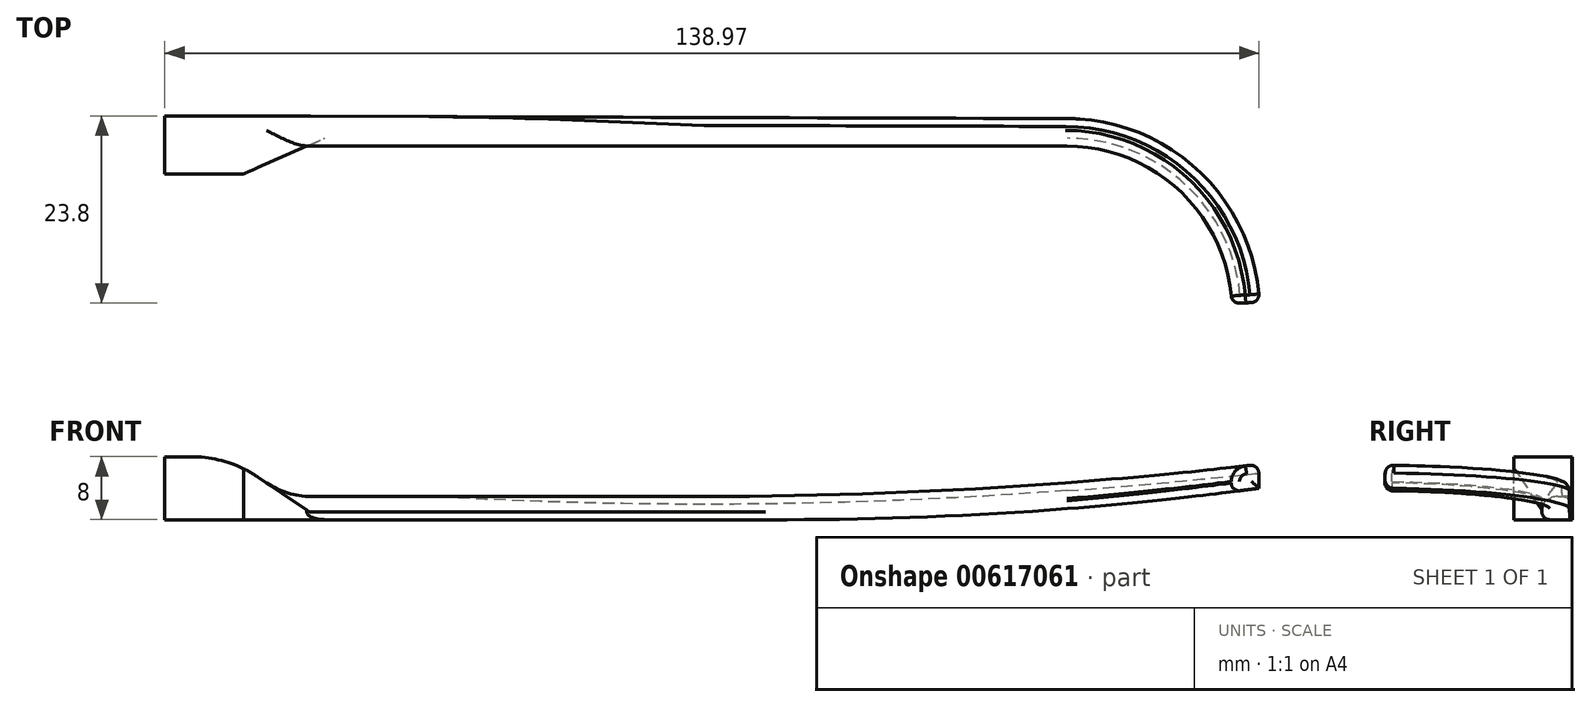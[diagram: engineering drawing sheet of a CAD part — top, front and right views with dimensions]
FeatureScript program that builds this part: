
annotation { "Feature Type Name" : "Feature", "Feature Type Description" : "" }
export const myFeature = defineFeature(function(context is Context, id is Id, definition is map)
    precondition{}
    {
        {
            var Q0;
            Q0=qCreatedBy(makeId("Front.planeOp"),FACE);
            var sketch = newSketch(context, id + "F0", { "sketchPlane" : qUnion([Q0])});
            skLineSegment(sketch, "E0.bottom", {"start": v(0, 0) * mm, "end": v(156.1, 0) * mm});
            skLineSegment(sketch, "E0.top", {"start": v(0, -43.39) * mm, "end": v(156.1, -43.39) * mm});
            skLineSegment(sketch, "E0.left", {"start": v(0, 0) * mm, "end": v(0, -43.39) * mm});
            skLineSegment(sketch, "E0.right", {"start": v(156.1, 0) * mm, "end": v(156.1, -43.39) * mm});
            skSolve(sketch);
        }
        {
            var Q0;
            Q0=qSketchRegion(id+"F0",true);
            extrude(context, id + "F1", {"entities" : qUnion([Q0]), "depth" : 50 * mm, "offsetDistance" : 25 * mm});
        }
        {
            var Q0;
            Q0=makeQuery(id+"F1.opExtrude","CAP_FACE",FACE,{"disambiguationData":[OSD([sQuery(id+"F0.wireOp",EDGE,"E0.bottom"),sQuery(id+"F0.wireOp",EDGE,"E0.top"),sQuery(id+"F0.wireOp",EDGE,"E0.left"),sQuery(id+"F0.wireOp",EDGE,"E0.right")])],"isStart":true});
            var sketch = newSketch(context, id + "F2", { "sketchPlane" : qUnion([Q0])});
            skLineSegment(sketch, "E1.bottom", {"start": v(-156.1, 0) * mm, "end": v(0, 0) * mm});
            skLineSegment(sketch, "E1.top", {"start": v(-156.1, -43.39) * mm, "end": v(0, -43.39) * mm});
            skLineSegment(sketch, "E1.left", {"start": v(-156.1, 0) * mm, "end": v(-156.1, -43.39) * mm});
            skLineSegment(sketch, "E1.right", {"start": v(0, 0) * mm, "end": v(0, -3.74) * mm});
            skLineSegment(sketch, "E2.trimOffspring", {"start": v(0, -25.02) * mm, "end": v(0, -43.39) * mm});
            skLineSegment(sketch, "E3.MirrorCS", {"start": v(0, -11.74) * mm, "end": v(-79.05, -11.74) * mm});
            skLineSegment(sketch, "E4.MirrorCS", {"start": v(-8, -3.74) * mm, "end": v(0, -3.74) * mm});
            skLineSegment(sketch, "E5.MirrorCS", {"start": v(-15.5, -8.8) * mm, "end": v(-8, -3.74) * mm});
            skLineSegment(sketch, "E6.MirrorCS", {"start": v(-68.52, -8.8) * mm, "end": v(-15.5, -8.8) * mm});
            skArc(sketch, "E7.MirrorCS", {"start": v(-68.52, -8.8) * mm, "mid": v(-104.19, -7.75) * mm, "end": v(-139.74, -4.62) * mm});
            skArc(sketch, "E8.MirrorCS", {"start": v(-79.05, -11.74) * mm, "mid": v(-109.6, -10.7) * mm, "end": v(-140, -7.61) * mm});
            skLineSegment(sketch, "E9.MirrorCS", {"start": v(-140, -7.61) * mm, "end": v(-139.74, -4.62) * mm});
            skLineSegment(sketch, "E10.trimOffspring", {"start": v(0, -11.74) * mm, "end": v(0, -25.02) * mm});
            skSolve(sketch);
        }
        {
            var Q0;
            Q0=qSketchRegion(id+"F2",true);
            extrude(context, id + "F3", {"entities" : qUnion([Q0]), "operationType" : NewBodyOperationType.REMOVE, "endBound" : BoundingType.THROUGH_ALL, "oppositeDirection" : true, "depth" : 25 * mm, "offsetDistance" : 25 * mm});
        }
        {
            var Q0;
            Q0=qCreatedBy(makeId("Top.planeOp"),FACE);
            var sketch = newSketch(context, id + "F4", { "sketchPlane" : qUnion([Q0])});
            skLineSegment(sketch, "E11", {"start": v(0, -7.38) * mm, "end": v(10, -7.38) * mm});
            skLineSegment(sketch, "E12", {"start": v(10, -7.38) * mm, "end": v(18.04, -3.85) * mm});
            skLineSegment(sketch, "E13", {"start": v(18.04, -3.85) * mm, "end": v(114.57, -3.85) * mm});
            skArc(sketch, "E14", {"start": v(135.54, -23.84) * mm, "mid": v(129.05, -9.65) * mm, "end": v(114.57, -3.85) * mm});
            skArc(sketch, "E15.0", {"start": v(139.03, -23.68) * mm, "mid": v(131.47, -7.12) * mm, "end": v(114.57, -0.35) * mm});
            skLineSegment(sketch, "E16", {"start": v(135.54, -23.84) * mm, "end": v(139.03, -23.68) * mm});
            skLineSegment(sketch, "E17", {"start": v(114.57, -0.35) * mm, "end": v(0, 0) * mm});
            skLineSegment(sketch, "E18.0", {"start": v(78.92, 0) * mm, "end": v(140, 0) * mm});
            skLineSegment(sketch, "E19.0", {"start": v(0, 0) * mm, "end": v(78.92, 0) * mm});
            skLineSegment(sketch, "E20.0", {"start": v(140, -50) * mm, "end": v(140, 0) * mm});
            skLineSegment(sketch, "E21.0", {"start": v(0, -50) * mm, "end": v(140, -50) * mm});
            skLineSegment(sketch, "E22.0", {"start": v(0, -50) * mm, "end": v(0, -50) * mm});
            skLineSegment(sketch, "E23.0", {"start": v(0, -50) * mm, "end": v(0, -7.38) * mm});
            skSolve(sketch);
        }
        {
            var Q0;
            Q0=qSketchRegion(id+"F4",true);
            extrude(context, id + "F5", {"entities" : qUnion([Q0]), "operationType" : NewBodyOperationType.REMOVE, "oppositeDirection" : true, "depth" : 25 * mm, "offsetDistance" : 25 * mm});
        }
        {
            var Q0;
            Q0=makeQuery(id+"F3.boolean.opBoolean","COPY",EDGE,{"derivedFrom":makeQuery(id+"F3.opExtrude","SWEPT_EDGE",EDGE,{"disambiguationData":[OSD([sQuery(id+"F2.wireOp",EDGE,"E4.MirrorCS"),sQuery(id+"F2.wireOp",EDGE,"E5.MirrorCS")])]})});
            fillet(context, id + "F6", {"entities" : qUnion([Q0]), "radius" : 15 * mm, "tangentPropagation" : true, "allowEdgeOverflow" : false});
        }
        {
            var Q0;
            Q0=makeQuery(id+"F3.boolean.opBoolean","COPY",EDGE,{"derivedFrom":makeQuery(id+"F3.opExtrude","SWEPT_EDGE",EDGE,{"disambiguationData":[OSD([sQuery(id+"F2.wireOp",EDGE,"E5.MirrorCS"),sQuery(id+"F2.wireOp",EDGE,"E6.MirrorCS")])]})});
            fillet(context, id + "F7", {"entities" : qUnion([Q0]), "radius" : 10 * mm, "tangentPropagation" : true, "allowEdgeOverflow" : false});
        }
        {
            var Q0;
            Q0=makeQuery(id+"F5.boolean.opBoolean","INTERSECT",EDGE,{"derivedFrom":[makeQuery(id+"F3.boolean.opBoolean","COPY",FACE,{"derivedFrom":makeQuery(id+"F3.opExtrude","SWEPT_FACE",FACE,{"disambiguationData":[OSD([sQuery(id+"F2.wireOp",EDGE,"E6.MirrorCS")])]})}),makeQuery(id+"F5.opExtrude","SWEPT_FACE",FACE,{"disambiguationData":[OSD([sQuery(id+"F4.wireOp",EDGE,"E13")])]})]});
            fillet(context, id + "F8", {"entities" : qUnion([Q0]), "radius" : 2 * mm, "tangentPropagation" : true, "allowEdgeOverflow" : false});
        }
        {
            var Q0;
            Q0=makeQuery(id+"F8.opFillet","BLEND_EDGE",EDGE,{"blendedFrom":[makeQuery(id+"F5.boolean.opBoolean","INTERSECT",EDGE,{"derivedFrom":[makeQuery(id+"F3.boolean.opBoolean","COPY",FACE,{"derivedFrom":makeQuery(id+"F3.opExtrude","SWEPT_FACE",FACE,{"disambiguationData":[OSD([sQuery(id+"F2.wireOp",EDGE,"E7.MirrorCS")])]})}),makeQuery(id+"F5.opExtrude","SWEPT_FACE",FACE,{"disambiguationData":[OSD([sQuery(id+"F4.wireOp",EDGE,"E14")])]})]}),makeQuery(id+"F5.boolean.opBoolean","COPY",FACE,{"derivedFrom":makeQuery(id+"F5.opExtrude","SWEPT_FACE",FACE,{"disambiguationData":[OSD([sQuery(id+"F4.wireOp",EDGE,"E16")])]})})],"blendedInto":[makeQuery(id+"F5.boolean.opBoolean","COPY",FACE,{"derivedFrom":makeQuery(id+"F5.opExtrude","SWEPT_FACE",FACE,{"disambiguationData":[OSD([sQuery(id+"F4.wireOp",EDGE,"E16")])]})})]});
            var Q1;
            Q1=makeQuery(id+"F5.boolean.opBoolean","INTERSECT",EDGE,{"derivedFrom":[makeQuery(id+"F3.boolean.opBoolean","COPY",FACE,{"derivedFrom":makeQuery(id+"F3.opExtrude","SWEPT_FACE",FACE,{"disambiguationData":[OSD([sQuery(id+"F2.wireOp",EDGE,"E7.MirrorCS")])]})}),makeQuery(id+"F5.opExtrude","SWEPT_FACE",FACE,{"disambiguationData":[OSD([sQuery(id+"F4.wireOp",EDGE,"E16")])]})]});
            var Q2;
            Q2=makeQuery(id+"F5.boolean.opBoolean","COPY",EDGE,{"derivedFrom":makeQuery(id+"F5.opExtrude","SWEPT_EDGE",EDGE,{"disambiguationData":[OSD([sQuery(id+"F4.wireOp",EDGE,"E15.0"),sQuery(id+"F4.wireOp",EDGE,"E16")])]})});
            var Q3;
            Q3=makeQuery(id+"F5.boolean.opBoolean","INTERSECT",EDGE,{"derivedFrom":[makeQuery(id+"F3.boolean.opBoolean","COPY",FACE,{"derivedFrom":makeQuery(id+"F3.opExtrude","SWEPT_FACE",FACE,{"disambiguationData":[OSD([sQuery(id+"F2.wireOp",EDGE,"E8.MirrorCS")])]})}),makeQuery(id+"F5.opExtrude","SWEPT_FACE",FACE,{"disambiguationData":[OSD([sQuery(id+"F4.wireOp",EDGE,"E16")])]})]});
            var Q4;
            Q4=makeQuery(id+"F5.boolean.opBoolean","INTERSECT",EDGE,{"derivedFrom":[makeQuery(id+"F3.boolean.opBoolean","COPY",FACE,{"derivedFrom":makeQuery(id+"F3.opExtrude","SWEPT_FACE",FACE,{"disambiguationData":[OSD([sQuery(id+"F2.wireOp",EDGE,"E7.MirrorCS")])]})}),makeQuery(id+"F5.opExtrude","SWEPT_FACE",FACE,{"disambiguationData":[OSD([sQuery(id+"F4.wireOp",EDGE,"E15.0")])]})]});
            var Q5;
            Q5=makeQuery(id+"F5.boolean.opBoolean","INTERSECT",EDGE,{"derivedFrom":[makeQuery(id+"F3.boolean.opBoolean","COPY",FACE,{"derivedFrom":makeQuery(id+"F3.opExtrude","SWEPT_FACE",FACE,{"disambiguationData":[OSD([sQuery(id+"F2.wireOp",EDGE,"E8.MirrorCS")])]})}),makeQuery(id+"F5.opExtrude","SWEPT_FACE",FACE,{"disambiguationData":[OSD([sQuery(id+"F4.wireOp",EDGE,"E14")])]})]});
            fillet(context, id + "F9", {"entities" : qUnion([Q0, Q1, Q2, Q3, Q4, Q5]), "radius" : 1 * mm, "tangentPropagation" : true, "allowEdgeOverflow" : false});
        }
    });
